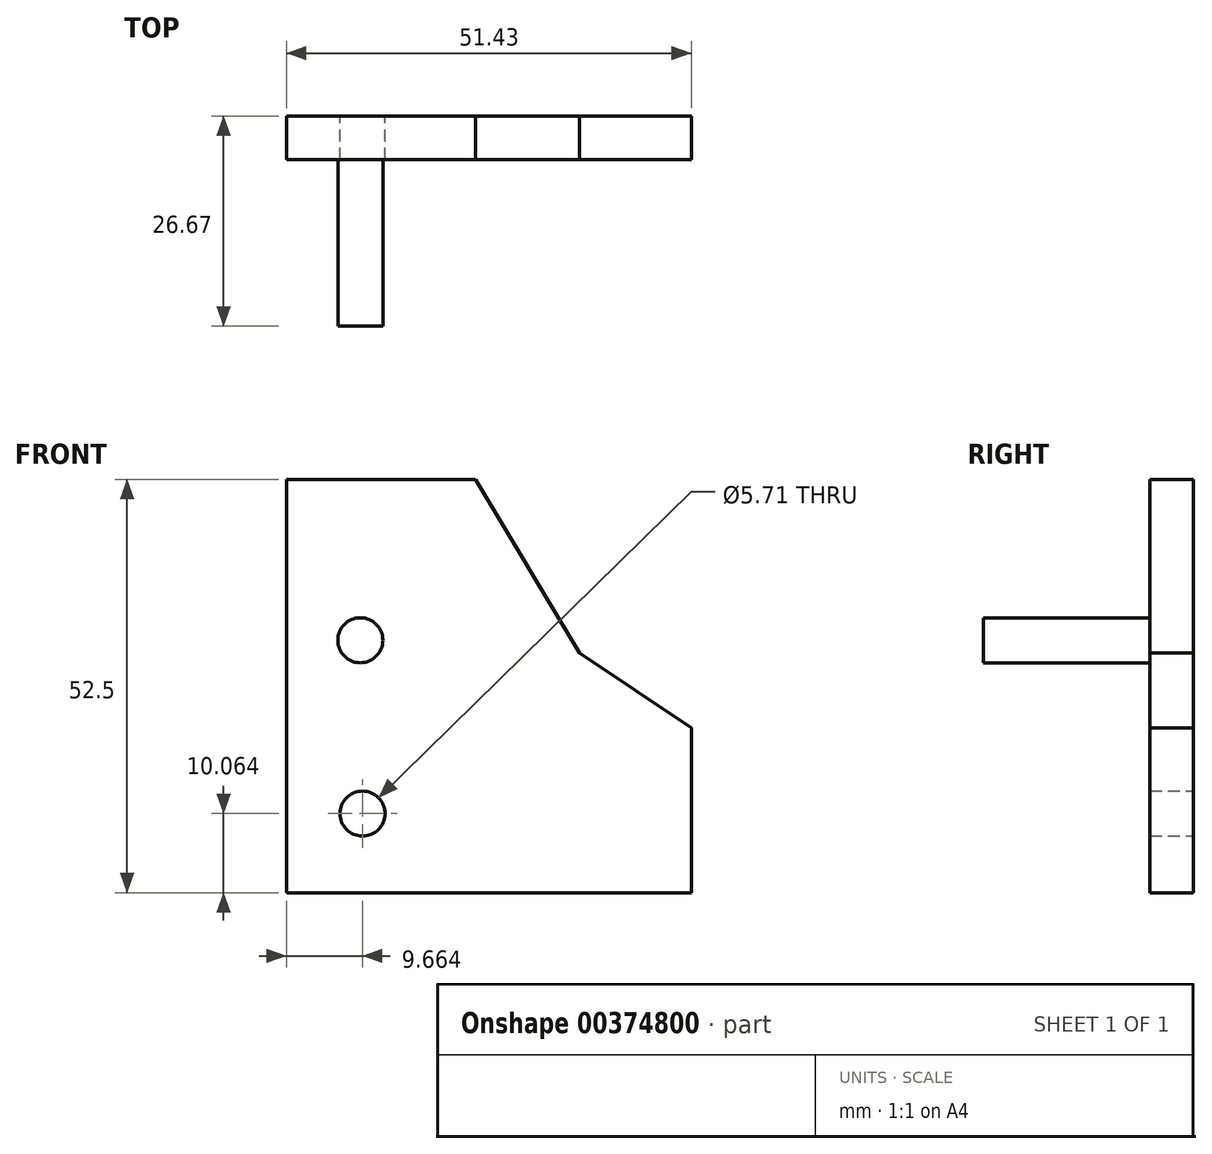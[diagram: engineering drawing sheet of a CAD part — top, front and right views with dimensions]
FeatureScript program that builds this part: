
annotation { "Feature Type Name" : "Feature", "Feature Type Description" : "" }
export const myFeature = defineFeature(function(context is Context, id is Id, definition is map)
    precondition{}
    {
        {
            var Q0;
            Q0=qCreatedBy(makeId("Front.planeOp"),FACE);
            var sketch = newSketch(context, id + "F0", { "sketchPlane" : qUnion([Q0])});
            skLineSegment(sketch, "E0", {"start": v(-6.67, 23.18) * mm, "end": v(-3.47, 23.18) * mm});
            skLineSegment(sketch, "E1", {"start": v(-6.67, 23.18) * mm, "end": v(-6.67, 16.18) * mm});
            skLineSegment(sketch, "E2", {"start": v(-3.47, 23.18) * mm, "end": v(-1.7, 20.25) * mm});
            skLineSegment(sketch, "E3", {"start": v(0.19, 18.98) * mm, "end": v(0.19, 16.18) * mm});
            skLineSegment(sketch, "E4", {"start": v(0.19, 16.18) * mm, "end": v(-6.67, 16.18) * mm});
            skLineSegment(sketch, "E5", {"start": v(-1.7, 20.25) * mm, "end": v(0.19, 18.98) * mm});
            skCircle(sketch, "E6", {"center": v(-5.38, 17.53) * mm, "radius": 0.38 * mm});
            skCircle(sketch, "E7", {"center": v(-5.42, 20.46) * mm, "radius": 0.38 * mm});
            skSolve(sketch);
        }
        {
            var Q0;
            Q0=makeQuery(id+"F0.imprint","IMPRINT",FACE,{"disambiguationData":[TD([[makeQuery(id+"F0.imprint","IMPRINT",EDGE,{"derivedFrom":sQuery(id+"F0.wireOp",EDGE,"E0")}),-1.0]])]});
            extrude(context, id + "F1", {"entities" : qUnion([Q0]), "depth" : 0.74 * mm, "offsetDistance" : 25.4 * mm});
        }
        {
            var Q0;
            Q0=makeQuery(id+"F0.imprint","IMPRINT",FACE,{"disambiguationData":[TD([[makeQuery(id+"F0.imprint","IMPRINT",EDGE,{"derivedFrom":sQuery(id+"F0.wireOp",EDGE,"E7")}),1.0]])]});
            extrude(context, id + "F2", {"entities" : qUnion([Q0]), "operationType" : NewBodyOperationType.ADD, "depth" : 3.56 * mm, "offsetDistance" : 25.4 * mm});
        }
        {
            var Q0;
            Q0=makeQuery(id+"F1.opExtrude","SWEPT_BODY",BODY,{"disambiguationData":[OSD([sQuery(id+"F0.wireOp",EDGE,"E0"),sQuery(id+"F0.wireOp",EDGE,"E1"),sQuery(id+"F0.wireOp",EDGE,"E2"),sQuery(id+"F0.wireOp",EDGE,"E3"),sQuery(id+"F0.wireOp",EDGE,"E4"),sQuery(id+"F0.wireOp",EDGE,"E5"),sQuery(id+"F0.wireOp",EDGE,"E6"),sQuery(id+"F0.wireOp",EDGE,"E7")])]});
            var Q1;
            Q1=qCreatedBy(makeId("Origin.pointOp"),VERTEX);
            transform(context, id + "F3", {"entities" : qUnion([Q0]), "transformType" : TransformType.SCALE_UNIFORMLY, "scale" : 7.5, "scalePoint" : qUnion([Q1]), "makeCopy" : false});
        }
    });
